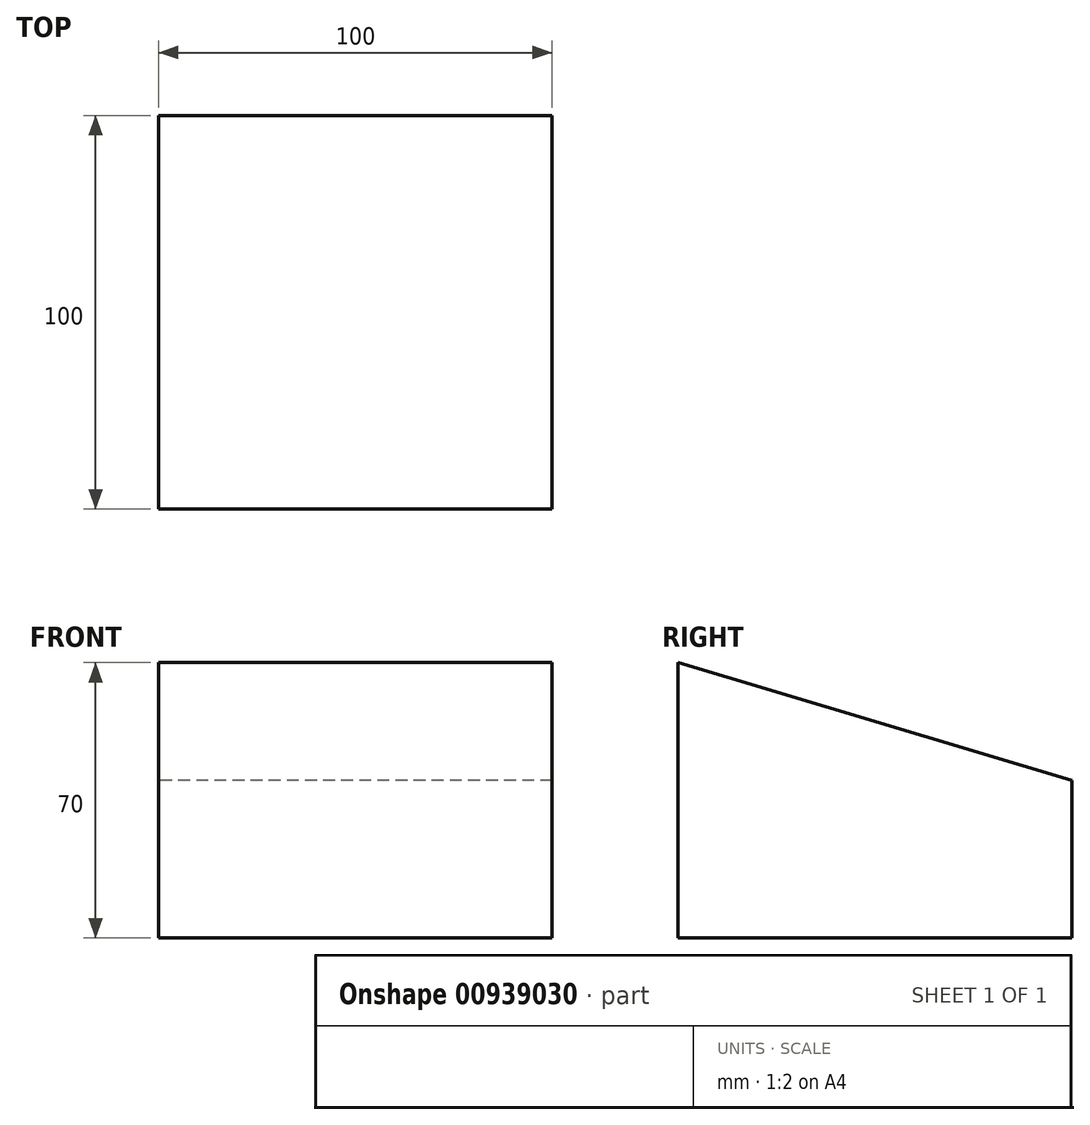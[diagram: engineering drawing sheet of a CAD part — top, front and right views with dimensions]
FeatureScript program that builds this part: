
annotation { "Feature Type Name" : "Feature", "Feature Type Description" : "" }
export const myFeature = defineFeature(function(context is Context, id is Id, definition is map)
    precondition{}
    {
        {
            var Q0;
            Q0=qCreatedBy(makeId("Top.planeOp"),FACE);
            var sketch = newSketch(context, id + "F0", { "sketchPlane" : qUnion([Q0])});
            skLineSegment(sketch, "E0.bottom", {"start": v(300, 300) * mm, "end": v(-300, 300) * mm});
            skLineSegment(sketch, "E0.top", {"start": v(300, -300) * mm, "end": v(-300, -300) * mm});
            skLineSegment(sketch, "E0.left", {"start": v(300, 300) * mm, "end": v(300, -300) * mm});
            skLineSegment(sketch, "E0.right", {"start": v(-300, 300) * mm, "end": v(-300, -300) * mm});
            skPoint(sketch, "E0.middle", {"position": v(0, 0) * mm});
            skSolve(sketch);
        }
        {
            var Q0;
            Q0=qCreatedBy(makeId("Top.planeOp"),FACE);
            var sketch = newSketch(context, id + "F1", { "sketchPlane" : qUnion([Q0])});
            skLineSegment(sketch, "E1.bottom", {"start": v(-300, 300) * mm, "end": v(-200, 300) * mm});
            skLineSegment(sketch, "E1.top", {"start": v(-300, 200) * mm, "end": v(-200, 200) * mm});
            skLineSegment(sketch, "E1.left", {"start": v(-300, 300) * mm, "end": v(-300, 200) * mm});
            skLineSegment(sketch, "E1.right", {"start": v(-200, 300) * mm, "end": v(-200, 200) * mm});
            skSolve(sketch);
        }
        {
            var Q0;
            Q0 = qSketchRegion(id + "F1", true);
            extrude(context, id + "F2", {"entities" : qUnion([Q0]), "depth" : 100 * mm, "offsetDistance" : 25 * mm});
        }
        {
            var Q0;
            Q0=makeQuery(id+"F2.opExtrude","SWEPT_FACE",FACE,{"disambiguationData":[OSD([sQuery(id+"F1.wireOp",EDGE,"E1.left")])]});
            var sketch = newSketch(context, id + "F3", { "sketchPlane" : qUnion([Q0])});
            skLineSegment(sketch, "E2", {"start": v(-300, 40) * mm, "end": v(-200, 70) * mm});
            skSolve(sketch);
        }
        {
            var Q0;
            {var subQ0=sQuery(id+"F3.wireOp",EDGE,"E2");Q0=makeQuery(id+"F3.imprint","IMPRINT",FACE,{"disambiguationData":[TD([[makeQuery(id+"F3.imprint","IMPRINT",EDGE,{"derivedFrom":subQ0}),1.0]])]});}
            extrude(context, id + "F4", {"entities" : qUnion([Q0]), "operationType" : NewBodyOperationType.REMOVE, "oppositeDirection" : true, "depth" : 154 * mm, "offsetDistance" : 25 * mm});
        }
    });
